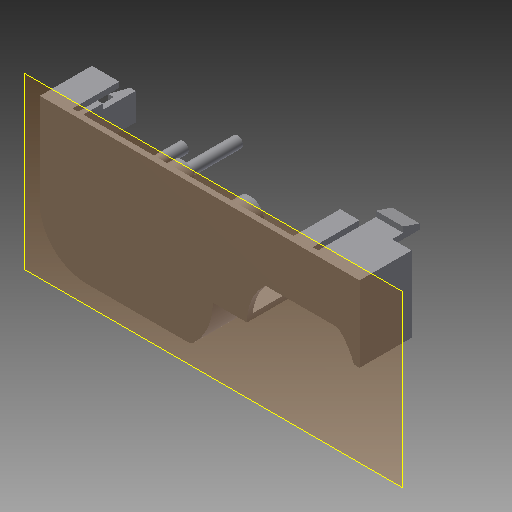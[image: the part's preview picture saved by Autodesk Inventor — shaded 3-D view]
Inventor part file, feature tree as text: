
AUTODESK INVENTOR PART (.ipt)
format: ipt  version: 2017 (Build 210142000, 142)  size: 256,000 bytes
history: native  units: mm
features: sketch x11, extrude x11, reference x7, plane x5
ambient origin geometry x8: Origin, YZ Plane, XZ Plane, XY Plane, X Axis, Y Axis, Z Axis, Center Point
bodies: Body1 (feature_tree)
feature tree (34):
  plane  "Work Plane1"
  sketch  "Sketch1"  dims[d2=10.0mm d3=0.0mm d4=10.0mm d5=0.0mm]
  plane  "Work Plane2"
  plane  "Work Plane3"
  extrude  "Extrusion2"  Depth=10.0mm TaperAngle=0.0deg
  sketch  "Sketch2"  dims[d6=10.0mm d7=0.0mm d8=10.0mm d9=0.0mm]
  plane  "Work Plane4"
  extrude  "Extrusion3"  Depth=10.0mm TaperAngle=0.0deg
  extrude  "Extrusion4"  Depth=1.0mm TaperAngle=0.0deg
  sketch  "Sketch4"  dims[d18=1.0mm d25=8.5mm d26=0.0mm]
  plane  "Work Plane5"
  extrude  "Extrusion5"  Depth=8.5mm TaperAngle=0.0deg
  extrude  "Extrusion6"  Depth=3.0mm
  extrude  "Extrusion7"  Depth=5.0mm TaperAngle=0.0deg
  extrude  "Extrusion9"  Depth=1.0mm
  extrude  "Extrusion12"  Depth=3.0mm
  extrude  "Extrusion13"  Depth=5.0mm TaperAngle=0.0deg
  extrude  "Extrusion14"  [1 undecoded]
  extrude  "Extrusion15"  [1 undecoded]
  reference  "Reference1"
  reference  "Reference2"
  sketch  "Sketch3"  dims[d10=10.0mm d11=0.0mm d16=1.0mm d17=0.0mm]
  reference  "Reference3"
  reference  "Reference4"
  sketch  "Sketch5"  dims[d51=6.0mm d52=0.0mm d53=3.0mm]
  reference  "Reference5"
  sketch  "Sketch6"  dims[d54=1.0mm d55=5.0mm d56=0.0mm]
  sketch  "Sketch7"  dims[d57=3.0mm d58=1.0mm]
  reference  "Reference7"
  reference  "Reference8"
  sketch  "Sketch11"  dims[d59=5.0mm d60=0.0mm d61=3.0mm]
  sketch  "Sketch12"  dims[d62=1.0mm d63=5.0mm d64=0.0mm]
  sketch  "Sketch13"
  sketch  "Sketch14"
note: 2 required parameter values undecoded (feature->parameter linkage not recoverable at this tier; creation-order binding heuristic only, values carry confidence <= 0.55)
